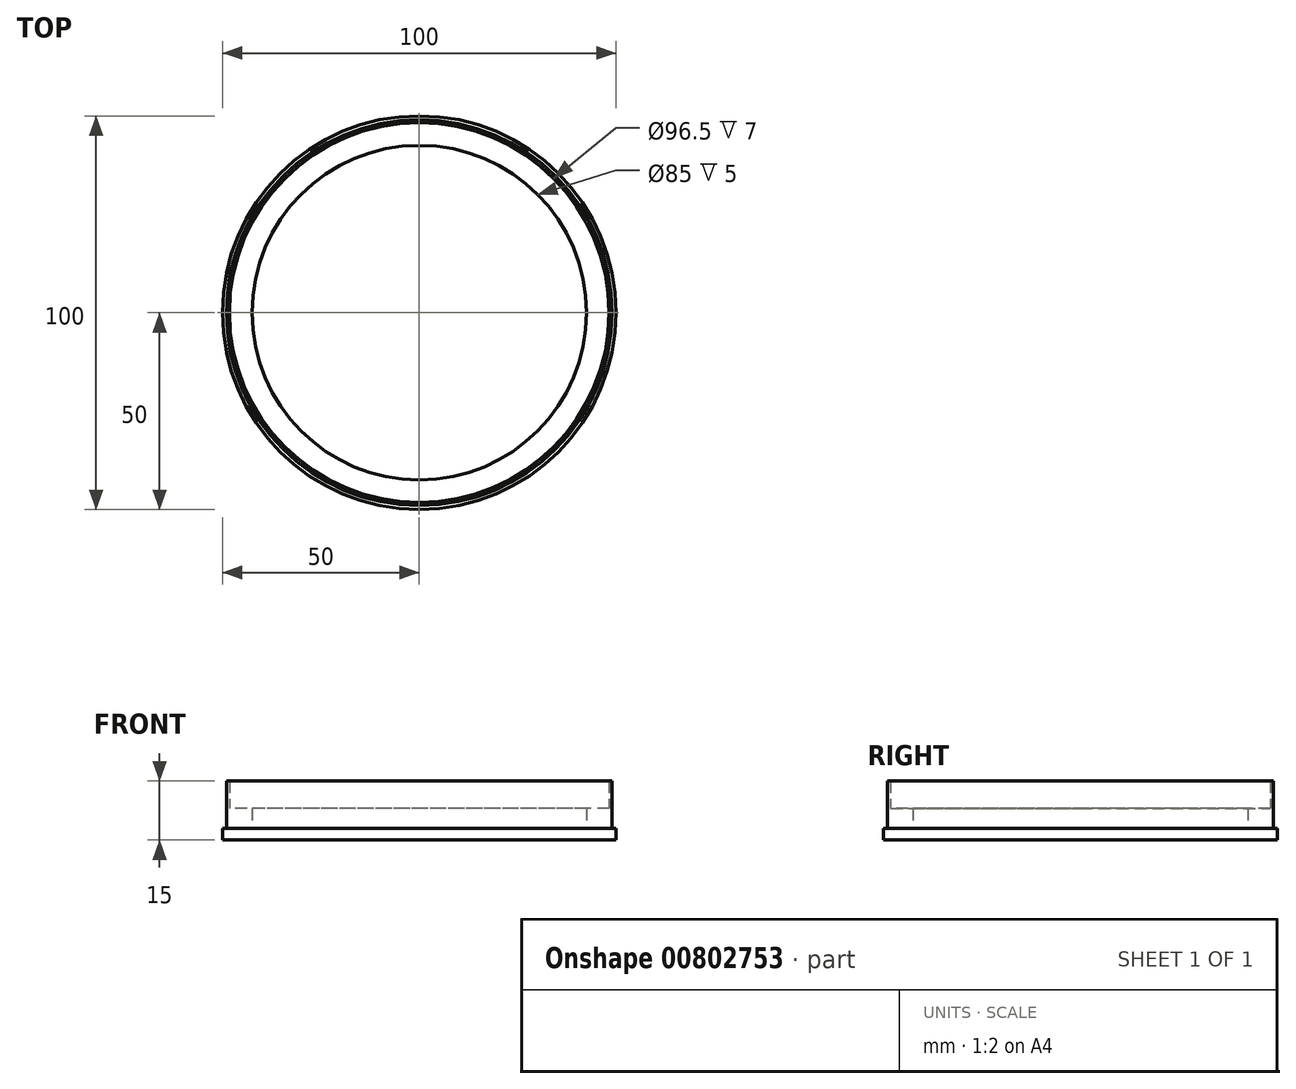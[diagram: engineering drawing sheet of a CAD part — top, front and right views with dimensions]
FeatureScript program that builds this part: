
annotation { "Feature Type Name" : "Feature", "Feature Type Description" : "" }
export const myFeature = defineFeature(function(context is Context, id is Id, definition is map)
    precondition{}
    {
        {
            var Q0;
            Q0=qCreatedBy(makeId("Top.planeOp"),FACE);
            var sketch = newSketch(context, id + "F0", { "sketchPlane" : qUnion([Q0])});
            skCircle(sketch, "E0", {"center": v(0, 0) * mm, "radius": 50 * mm});
            skSolve(sketch);
        }
        {
            var Q0;
            Q0 = qSketchRegion(id + "F0", true);
            extrude(context, id + "F1", {"entities" : qUnion([Q0]), "depth" : 3 * mm, "offsetDistance" : 25 * mm});
        }
        {
            var Q0;
            Q0=makeQuery(id+"F1.opExtrude","CAP_FACE",FACE,{"disambiguationData":[OSD([sQuery(id+"F0.wireOp",EDGE,"E0")])],"isStart":false});
            var sketch = newSketch(context, id + "F2", { "sketchPlane" : qUnion([Q0])});
            skCircle(sketch, "E1", {"center": v(0, 0) * mm, "radius": 49 * mm});
            skCircle(sketch, "E2", {"center": v(0, 0) * mm, "radius": 42.5 * mm});
            skSolve(sketch);
        }
        {
            var Q0;
            Q0 = qSketchRegion(id + "F2", true);
            extrude(context, id + "F3", {"entities" : qUnion([Q0]), "operationType" : NewBodyOperationType.ADD, "depth" : 5 * mm, "offsetDistance" : 25 * mm});
        }
        {
            var Q0;
            Q0=makeQuery(id+"F3.opExtrude","CAP_FACE",FACE,{"disambiguationData":[OSD([sQuery(id+"F2.wireOp",EDGE,"E1"),sQuery(id+"F2.wireOp",EDGE,"E2")])],"isStart":false});
            var sketch = newSketch(context, id + "F4", { "sketchPlane" : qUnion([Q0])});
            skCircle(sketch, "E3", {"center": v(0, 0) * mm, "radius": 49 * mm});
            skCircle(sketch, "E4", {"center": v(0, 0) * mm, "radius": 48.25 * mm});
            skSolve(sketch);
        }
        {
            var Q0;
            Q0 = qSketchRegion(id + "F4", true);
            extrude(context, id + "F5", {"entities" : qUnion([Q0]), "operationType" : NewBodyOperationType.ADD, "depth" : 7 * mm, "offsetDistance" : 25 * mm});
        }
    });
